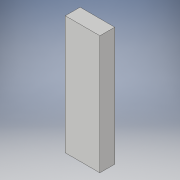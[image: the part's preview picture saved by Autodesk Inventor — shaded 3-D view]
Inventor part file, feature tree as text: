
AUTODESK INVENTOR PART (.ipt)
format: ipt  version: 2017 (Build 210142000, 142)  size: 89,088 bytes
history: native  units: in
note: dims shown in document units (in); Inventor stores cm internally (conversion verified against a paired STEP export)
features: extrude x1, sketch x1
ambient origin geometry x8: Origin, YZ Plane, XZ Plane, XY Plane, X Axis, Y Axis, Z Axis, Center Point
bodies: Solid1 (feature_tree)
feature tree (2):
  extrude  "Extrusion1"  Depth=1.5in
  sketch  "Sketch1"  dims[d0=3.5in d1=1.5in d2=12.0in d3=0.0in]
